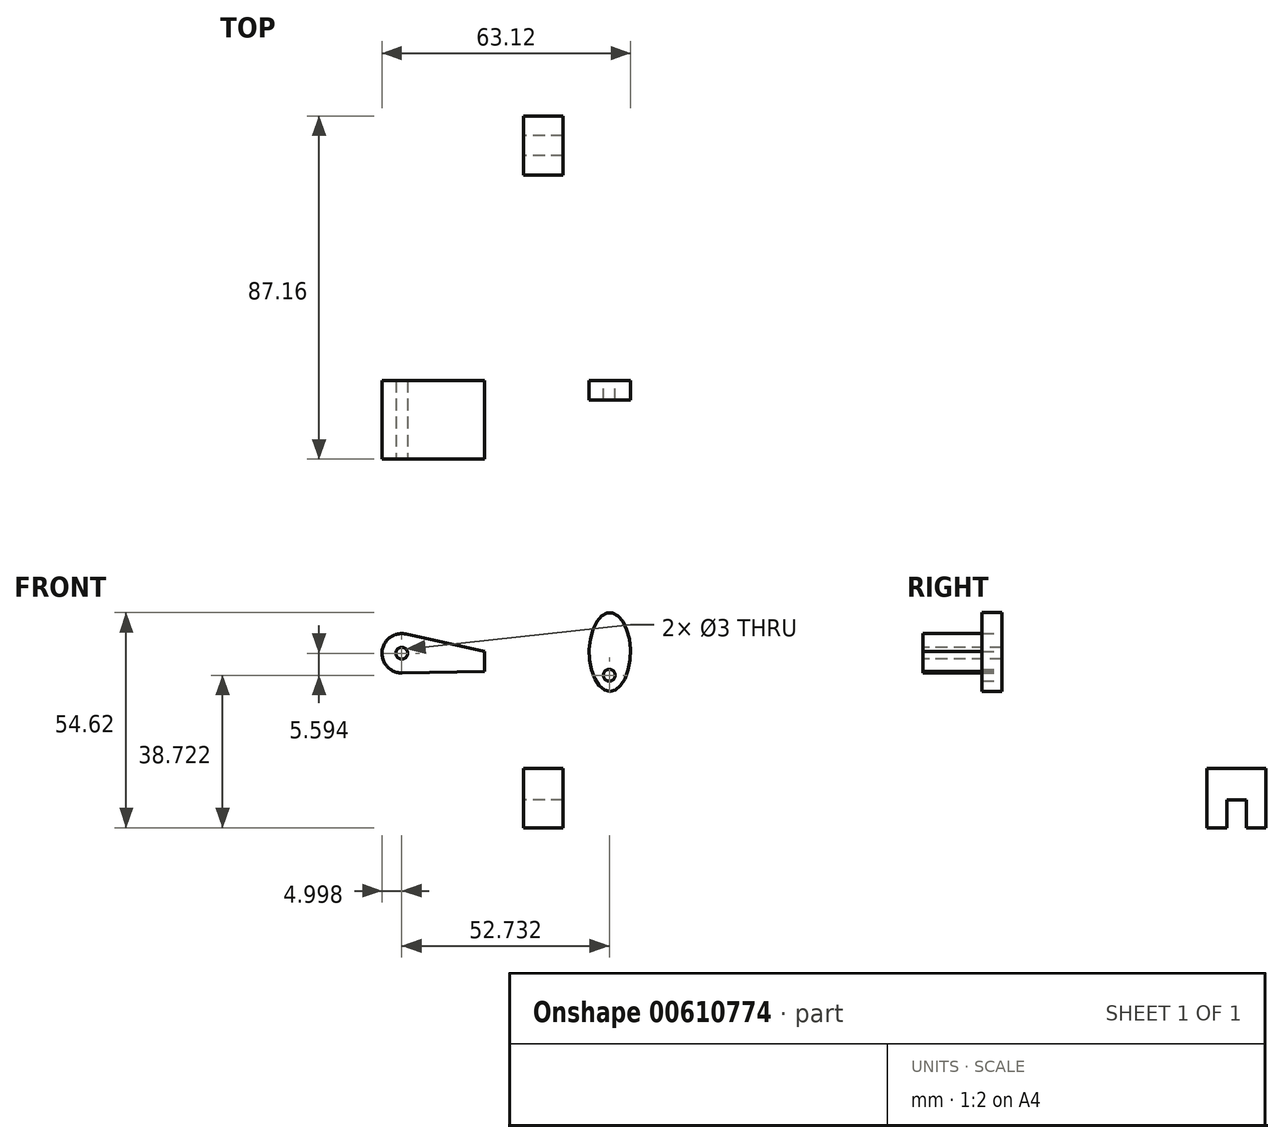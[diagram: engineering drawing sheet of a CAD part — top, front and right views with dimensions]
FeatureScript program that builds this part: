
annotation { "Feature Type Name" : "Feature", "Feature Type Description" : "" }
export const myFeature = defineFeature(function(context is Context, id is Id, definition is map)
    precondition{}
    {
        {
            var Q0;
            Q0=qCreatedBy(makeId("Front.planeOp"),FACE);
            var sketch = newSketch(context, id + "F0", { "sketchPlane" : qUnion([Q0])});
            skCircle(sketch, "E0", {"center": v(-30.95, 37.3) * mm, "radius": 5 * mm});
            skLineSegment(sketch, "E1", {"start": v(-29.86, 42.18) * mm, "end": v(-9.86, 37.7) * mm});
            skLineSegment(sketch, "E2", {"start": v(-9.86, 37.7) * mm, "end": v(-9.86, 32.7) * mm});
            skLineSegment(sketch, "E3", {"start": v(-9.86, 32.7) * mm, "end": v(-30.86, 32.3) * mm});
            skSolve(sketch);
        }
        {
            var Q0;
            Q0 = qSketchRegion(id + "F0", true);
            extrude(context, id + "F1", {"entities" : qUnion([Q0]), "depth" : 20 * mm, "offsetDistance" : 25 * mm});
        }
        {
            var Q0;
            Q0=makeQuery(id+"F1.opExtrude","CAP_FACE",FACE,{"disambiguationData":[OSD([sQuery(id+"F0.wireOp",EDGE,"E0"),sQuery(id+"F0.wireOp",EDGE,"E1"),sQuery(id+"F0.wireOp",EDGE,"E2"),sQuery(id+"F0.wireOp",EDGE,"E3")])],"isStart":false});
            var sketch = newSketch(context, id + "F2", { "sketchPlane" : qUnion([Q0])});
            skCircle(sketch, "E4", {"center": v(-30.95, 37.3) * mm, "radius": 1.5 * mm});
            skSolve(sketch);
        }
        {
            var Q0;
            Q0=sQuery(id+"F2.wireOp",VERTEX,"E4.center");
            var Q1;
            Q1=makeQuery(id+"F1.opExtrude","SWEPT_BODY",BODY,{"disambiguationData":[OSD([sQuery(id+"F0.wireOp",EDGE,"E0"),sQuery(id+"F0.wireOp",EDGE,"E1"),sQuery(id+"F0.wireOp",EDGE,"E2"),sQuery(id+"F0.wireOp",EDGE,"E3")])]});
            hole(context, id + "F3", {"style" : HoleStyle.SIMPLE, "endStyle" : HoleEndStyle.THROUGH, "holeDiameter" : 3 * mm, "majorDiameter" : 5 * mm, "isTappedThrough" : true, "tappedDepth" : 12 * mm, "tapClearance" : 3, "locations" : qUnion([Q0]), "scope" : qUnion([Q1])});
        }
        {
            var Q0;
            Q0=qCreatedBy(makeId("Front.planeOp"),FACE);
            var sketch = newSketch(context, id + "F4", { "sketchPlane" : qUnion([Q0])});
            skEllipse(sketch, "E5", {"center": v(21.93, 37.6) * mm, "majorRadius": 10 * mm, "minorRadius": 5.24 * mm, "majorAxis": v(0, -1)});
            skSolve(sketch);
        }
        {
            var Q0;
            Q0=makeQuery(id+"F4.imprint","IMPRINT",FACE,{"disambiguationData":[TD([[makeQuery(id+"F4.imprint","IMPRINT",EDGE,{"derivedFrom":sQuery(id+"F4.wireOp",EDGE,"E5")}),1.0]])]});
            var sketch = newSketch(context, id + "F5", { "sketchPlane" : qUnion([Q0])});
            skCircle(sketch, "E6", {"center": v(21.78, 31.7) * mm, "radius": 1.5 * mm});
            skSolve(sketch);
        }
        {
            var Q0;
            Q0 = qSketchRegion(id + "F4", true);
            extrude(context, id + "F6", {"entities" : qUnion([Q0]), "depth" : 5 * mm, "offsetDistance" : 25 * mm});
        }
        {
            var Q0;
            Q0=sQuery(id+"F5.wireOp",VERTEX,"E6.center");
            var Q1;
            Q1=makeQuery(id+"F6.opExtrude","SWEPT_BODY",BODY,{"disambiguationData":[OSD([sQuery(id+"F4.wireOp",EDGE,"E5")])]});
            hole(context, id + "F7", {"style" : HoleStyle.SIMPLE, "endStyle" : HoleEndStyle.THROUGH, "oppositeDirection" : true, "holeDiameter" : 3 * mm, "majorDiameter" : 5 * mm, "isTappedThrough" : true, "tappedDepth" : 12 * mm, "tapClearance" : 3, "locations" : qUnion([Q0]), "scope" : qUnion([Q1])});
        }
        {
            var Q0;
            Q0=qCreatedBy(makeId("Right.planeOp"),FACE);
            var sketch = newSketch(context, id + "F8", { "sketchPlane" : qUnion([Q0])});
            skLineSegment(sketch, "E7", {"start": v(62.16, 0) * mm, "end": v(57.16, 0) * mm});
            skLineSegment(sketch, "E8", {"start": v(57.16, 0) * mm, "end": v(57.16, -7.02) * mm});
            skLineSegment(sketch, "E9", {"start": v(57.16, -7.02) * mm, "end": v(52.16, -7.02) * mm});
            skLineSegment(sketch, "E10", {"start": v(52.16, -7.02) * mm, "end": v(52.16, 7.98) * mm});
            skLineSegment(sketch, "E11", {"start": v(52.16, 7.98) * mm, "end": v(67.16, 7.98) * mm});
            skLineSegment(sketch, "E12", {"start": v(67.16, 7.98) * mm, "end": v(67.16, -7.02) * mm});
            skLineSegment(sketch, "E13", {"start": v(67.16, -7.02) * mm, "end": v(62.16, -7.02) * mm});
            skLineSegment(sketch, "E14", {"start": v(62.16, -7.02) * mm, "end": v(62.16, 0) * mm});
            skSolve(sketch);
        }
        {
            var Q0;
            Q0 = qSketchRegion(id + "F8", true);
            extrude(context, id + "F9", {"entities" : qUnion([Q0]), "depth" : 10 * mm, "offsetDistance" : 25 * mm});
        }
    });
